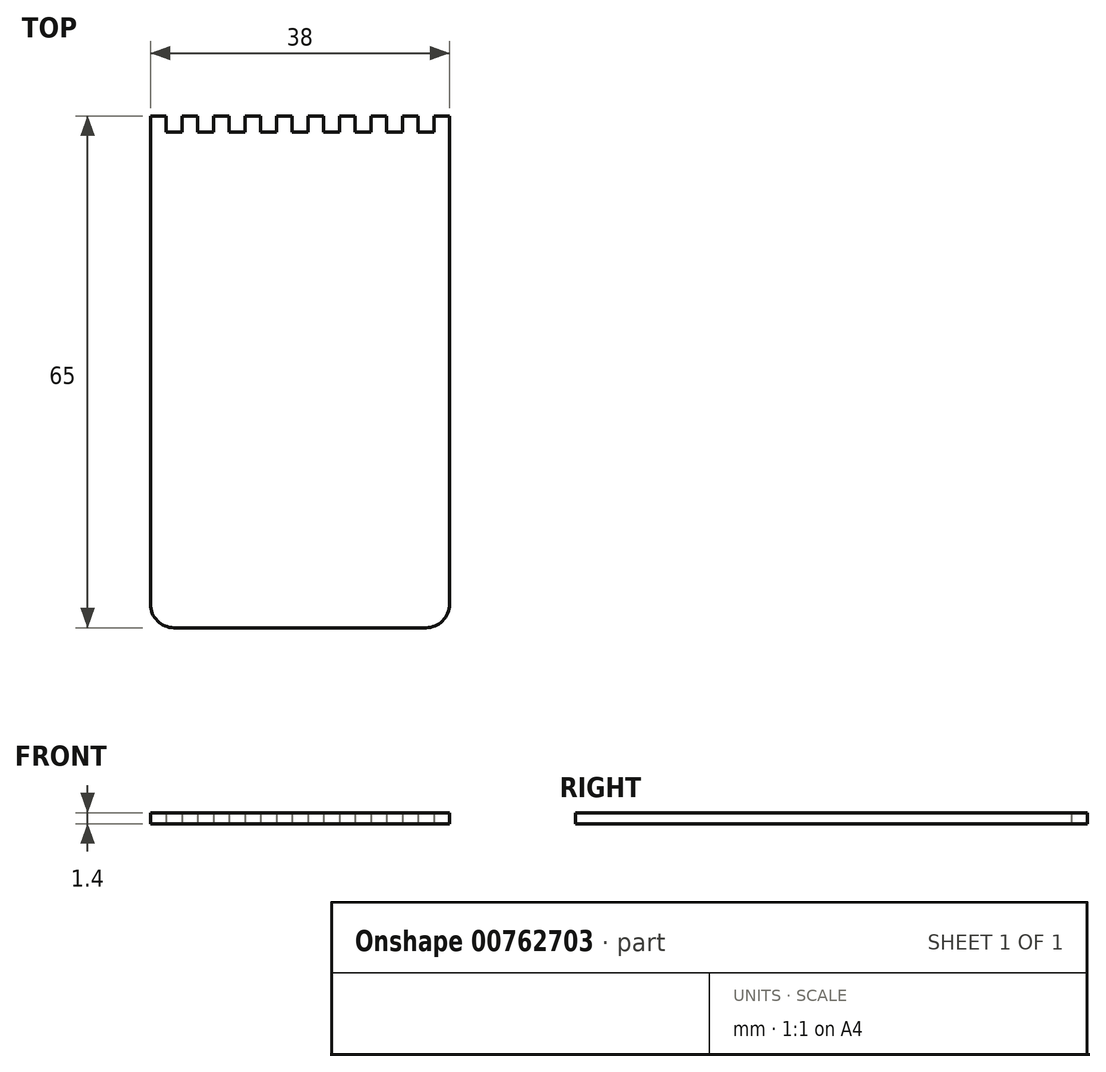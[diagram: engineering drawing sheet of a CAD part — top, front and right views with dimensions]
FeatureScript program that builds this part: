
annotation { "Feature Type Name" : "Feature", "Feature Type Description" : "" }
export const myFeature = defineFeature(function(context is Context, id is Id, definition is map)
    precondition{}
    {
        {
            var Q0;
            Q0=qCreatedBy(makeId("Top.planeOp"),FACE);
            var sketch = newSketch(context, id + "F0", { "sketchPlane" : qUnion([Q0])});
            skPoint(sketch, "E0.middle", {"position": v(0, 0) * mm});
            skLineSegment(sketch, "E1.left", {"start": v(-20, 75) * mm, "end": v(-20, 13) * mm});
            skPoint(sketch, "E1.middle", {"position": v(0, 50) * mm});
            skLineSegment(sketch, "E2.bottom", {"start": v(-20, 75) * mm, "end": v(-18, 75) * mm});
            skLineSegment(sketch, "E2.left", {"start": v(-20, 75) * mm, "end": v(-20, 73) * mm});
            skLineSegment(sketch, "E2.right", {"start": v(-18, 75) * mm, "end": v(-18, 73) * mm});
            skLineSegment(sketch, "E3.top", {"start": v(-18, 73) * mm, "end": v(-16, 73) * mm});
            skLineSegment(sketch, "E3.right", {"start": v(-16, 75) * mm, "end": v(-16, 73) * mm});
            skLineSegment(sketch, "E4.bottom", {"start": v(-16, 75) * mm, "end": v(-14, 75) * mm});
            skLineSegment(sketch, "E4.right", {"start": v(-14, 75) * mm, "end": v(-14, 73) * mm});
            skLineSegment(sketch, "E5.bottom", {"start": v(-14, 73) * mm, "end": v(-12, 73) * mm});
            skLineSegment(sketch, "E5.left", {"start": v(-14, 73) * mm, "end": v(-14, 75) * mm});
            skLineSegment(sketch, "E5.right", {"start": v(-12, 73) * mm, "end": v(-12, 75) * mm});
            skLineSegment(sketch, "E6.bottom", {"start": v(-12, 75) * mm, "end": v(-10, 75) * mm});
            skLineSegment(sketch, "E6.left", {"start": v(-12, 75) * mm, "end": v(-12, 73) * mm});
            skLineSegment(sketch, "E6.right", {"start": v(-10, 75) * mm, "end": v(-10, 73) * mm});
            skLineSegment(sketch, "E7.bottom", {"start": v(-10, 73) * mm, "end": v(-8, 73) * mm});
            skLineSegment(sketch, "E7.left", {"start": v(-10, 73) * mm, "end": v(-10, 75) * mm});
            skLineSegment(sketch, "E7.right", {"start": v(-8, 73) * mm, "end": v(-8, 75) * mm});
            skLineSegment(sketch, "E8.bottom", {"start": v(-8, 75) * mm, "end": v(-6, 75) * mm});
            skLineSegment(sketch, "E8.left", {"start": v(-8, 75) * mm, "end": v(-8, 73) * mm});
            skLineSegment(sketch, "E8.right", {"start": v(-6, 75) * mm, "end": v(-6, 73) * mm});
            skLineSegment(sketch, "E9.bottom", {"start": v(-6, 73) * mm, "end": v(-4, 73) * mm});
            skLineSegment(sketch, "E9.left", {"start": v(-6, 73) * mm, "end": v(-6, 75) * mm});
            skLineSegment(sketch, "E9.right", {"start": v(-4, 73) * mm, "end": v(-4, 75) * mm});
            skLineSegment(sketch, "E10.bottom", {"start": v(-4, 75) * mm, "end": v(-2, 75) * mm});
            skLineSegment(sketch, "E10.left", {"start": v(-4, 75) * mm, "end": v(-4, 73) * mm});
            skLineSegment(sketch, "E10.right", {"start": v(-2, 75) * mm, "end": v(-2, 73) * mm});
            skLineSegment(sketch, "E11.bottom", {"start": v(-2, 73) * mm, "end": v(0, 73) * mm});
            skLineSegment(sketch, "E11.left", {"start": v(-2, 73) * mm, "end": v(-2, 75) * mm});
            skLineSegment(sketch, "E11.right", {"start": v(0, 73) * mm, "end": v(0, 75) * mm});
            skLineSegment(sketch, "E12.bottom", {"start": v(0, 75) * mm, "end": v(2, 75) * mm});
            skLineSegment(sketch, "E12.left", {"start": v(0, 75) * mm, "end": v(0, 73) * mm});
            skLineSegment(sketch, "E12.right", {"start": v(2, 75) * mm, "end": v(2, 73) * mm});
            skLineSegment(sketch, "E13.bottom", {"start": v(2, 73) * mm, "end": v(4, 73) * mm});
            skLineSegment(sketch, "E13.left", {"start": v(2, 73) * mm, "end": v(2, 75) * mm});
            skLineSegment(sketch, "E13.right", {"start": v(4, 73) * mm, "end": v(4, 75) * mm});
            skLineSegment(sketch, "E14.bottom", {"start": v(4, 75) * mm, "end": v(6, 75) * mm});
            skLineSegment(sketch, "E14.left", {"start": v(4, 75) * mm, "end": v(4, 73) * mm});
            skLineSegment(sketch, "E14.right", {"start": v(6, 75) * mm, "end": v(6, 73) * mm});
            skLineSegment(sketch, "E15.bottom", {"start": v(6, 73) * mm, "end": v(8, 73) * mm});
            skLineSegment(sketch, "E15.left", {"start": v(6, 73) * mm, "end": v(6, 75) * mm});
            skLineSegment(sketch, "E15.right", {"start": v(8, 73) * mm, "end": v(8, 75) * mm});
            skLineSegment(sketch, "E16.bottom", {"start": v(8, 75) * mm, "end": v(10, 75) * mm});
            skLineSegment(sketch, "E16.left", {"start": v(8, 75) * mm, "end": v(8, 73) * mm});
            skLineSegment(sketch, "E16.right", {"start": v(10, 75) * mm, "end": v(10, 73) * mm});
            skLineSegment(sketch, "E17.bottom", {"start": v(10, 73) * mm, "end": v(12, 73) * mm});
            skLineSegment(sketch, "E17.left", {"start": v(10, 73) * mm, "end": v(10, 75) * mm});
            skLineSegment(sketch, "E17.right", {"start": v(12, 73) * mm, "end": v(12, 75) * mm});
            skLineSegment(sketch, "E18.bottom", {"start": v(12, 75) * mm, "end": v(14, 75) * mm});
            skLineSegment(sketch, "E18.left", {"start": v(12, 75) * mm, "end": v(12, 73) * mm});
            skLineSegment(sketch, "E18.right", {"start": v(14, 75) * mm, "end": v(14, 73) * mm});
            skLineSegment(sketch, "E19.bottom", {"start": v(14, 73) * mm, "end": v(16, 73) * mm});
            skLineSegment(sketch, "E19.left", {"start": v(14, 73) * mm, "end": v(14, 75) * mm});
            skLineSegment(sketch, "E19.right", {"start": v(16, 73) * mm, "end": v(16, 75) * mm});
            skLineSegment(sketch, "E20.bottom", {"start": v(16, 75) * mm, "end": v(18, 75) * mm});
            skLineSegment(sketch, "E20.left", {"start": v(16, 75) * mm, "end": v(16, 73) * mm});
            skLineSegment(sketch, "E20.right", {"start": v(18, 75) * mm, "end": v(18, 73) * mm});
            skLineSegment(sketch, "E21", {"start": v(18, 73) * mm, "end": v(18, 13) * mm});
            skLineSegment(sketch, "E22", {"start": v(-17, 10) * mm, "end": v(-13, 10) * mm});
            skLineSegment(sketch, "E23", {"start": v(13, 10) * mm, "end": v(15, 10) * mm});
            skPoint(sketch, "E24.visualSharp", {"position": v(-10, -50) * mm});
            skPoint(sketch, "E25.visualSharp", {"position": v(10, -50) * mm});
            skPoint(sketch, "E26.visualSharp", {"position": v(18, 10) * mm});
            skArc(sketch, "E26.filletArc", {"start": v(15, 10) * mm, "mid": v(17.12, 10.88) * mm, "end": v(18, 13) * mm});
            skPoint(sketch, "E27.visualSharp", {"position": v(-20, 10) * mm});
            skArc(sketch, "E27.filletArc", {"start": v(-20, 13) * mm, "mid": v(-19.12, 10.88) * mm, "end": v(-17, 10) * mm});
            skPoint(sketch, "E28.visualSharp", {"position": v(10, 10) * mm});
            skPoint(sketch, "E29.visualSharp", {"position": v(-10, 10) * mm});
            skLineSegment(sketch, "E30", {"start": v(-13, 10) * mm, "end": v(13, 10) * mm});
            skSolve(sketch);
        }
        {
            var Q0;
            {var subQ0=sQuery(id+"F0.wireOp",EDGE,"E2.bottom");Q0=makeQuery(id+"F0.imprint","IMPRINT",FACE,{"disambiguationData":[TD([[makeQuery(id+"F0.imprint","IMPRINT",EDGE,{"derivedFrom":subQ0}),-1.0]])]});}
            extrude(context, id + "F1", {"entities" : qUnion([Q0]), "depth" : 1.4 * mm, "offsetDistance" : 25 * mm});
        }
    });
